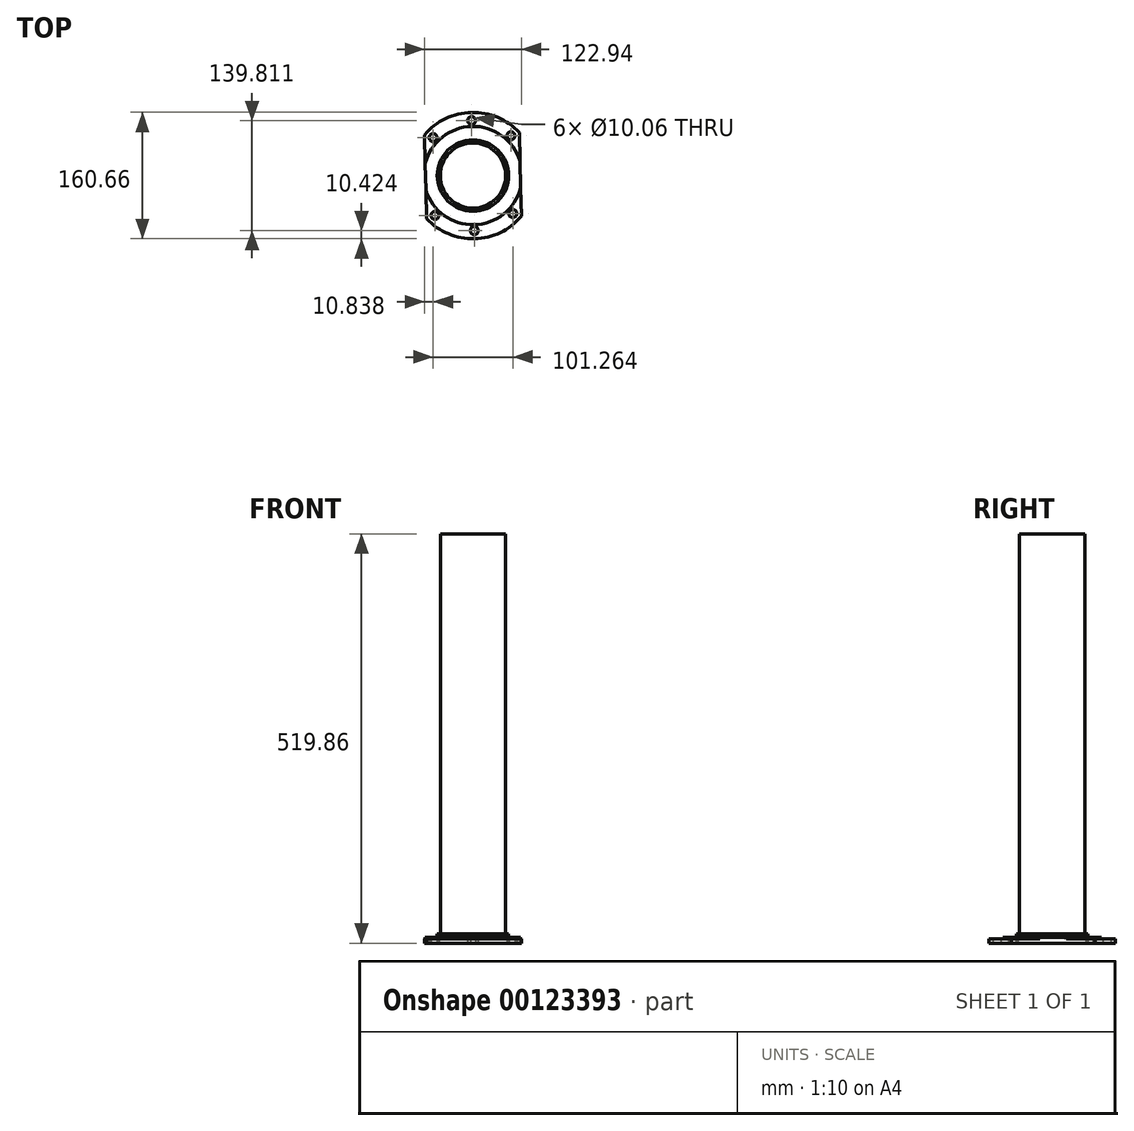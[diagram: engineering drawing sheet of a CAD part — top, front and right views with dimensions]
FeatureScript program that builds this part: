
annotation { "Feature Type Name" : "Feature", "Feature Type Description" : "" }
export const myFeature = defineFeature(function(context is Context, id is Id, definition is map)
    precondition{}
    {
        {
            var Q0;
            Q0=qCreatedBy(makeId("Top.planeOp"),FACE);
            var sketch = newSketch(context, id + "F0", { "sketchPlane" : qUnion([Q0])});
            skCircle(sketch, "E0", {"center": v(0, 0) * mm, "radius": 45.38 * mm, "construction": true});
            skCircle(sketch, "E1", {"center": v(0, 0) * mm, "radius": 69.93 * mm, "construction": true});
            skLineSegment(sketch, "E2", {"start": v(58.89, 54.63) * mm, "end": v(61.47, -51.7) * mm});
            skLineSegment(sketch, "E3", {"start": v(-61.47, 51.7) * mm, "end": v(-58.89, -54.63) * mm});
            skCircle(sketch, "E4", {"center": v(48.23, 50.63) * mm, "radius": 5.03 * mm});
            skCircle(sketch, "E5", {"center": v(-1.7, 69.9) * mm, "radius": 5.03 * mm});
            skCircle(sketch, "E6", {"center": v(-50.63, 48.23) * mm, "radius": 5.03 * mm});
            skCircle(sketch, "E7", {"center": v(50.63, -48.23) * mm, "radius": 5.03 * mm});
            skCircle(sketch, "E8", {"center": v(1.7, -69.9) * mm, "radius": 5.03 * mm});
            skCircle(sketch, "E9", {"center": v(-48.23, -50.63) * mm, "radius": 5.03 * mm});
            skLineSegment(sketch, "E10", {"start": v(48.23, 50.63) * mm, "end": v(50.63, -48.23) * mm, "construction": true});
            skLineSegment(sketch, "E11", {"start": v(-1.7, 69.9) * mm, "end": v(1.7, -69.9) * mm, "construction": true});
            skLineSegment(sketch, "E12", {"start": v(-50.63, 48.23) * mm, "end": v(-48.23, -50.63) * mm, "construction": true});
            skLineSegment(sketch, "E13", {"start": v(48.23, 50.63) * mm, "end": v(-48.23, -50.63) * mm, "construction": true});
            skLineSegment(sketch, "E14", {"start": v(50.63, -48.23) * mm, "end": v(-50.63, 48.23) * mm, "construction": true});
            skArc(sketch, "E15", {"start": v(58.89, 54.63) * mm, "mid": v(-1.95, 80.3) * mm, "end": v(-61.47, 51.7) * mm});
            skArc(sketch, "E16.trimOffspring", {"start": v(-58.89, -54.63) * mm, "mid": v(1.95, -80.3) * mm, "end": v(61.47, -51.7) * mm});
            skSolve(sketch);
        }
        {
            var Q0;
            Q0 = qSketchRegion(id + "F0", true);
            extrude(context, id + "F1", {"entities" : qUnion([Q0]), "depth" : 5.5 * mm});
        }
        {
            var Q0;
            Q0=makeQuery(id+"F1.opExtrude","CAP_FACE",FACE,{"disambiguationData":[OSD([sQuery(id+"F0.wireOp",EDGE,"E2"),sQuery(id+"F0.wireOp",EDGE,"E3"),sQuery(id+"F0.wireOp",EDGE,"E4"),sQuery(id+"F0.wireOp",EDGE,"E5"),sQuery(id+"F0.wireOp",EDGE,"E6"),sQuery(id+"F0.wireOp",EDGE,"E7"),sQuery(id+"F0.wireOp",EDGE,"E8"),sQuery(id+"F0.wireOp",EDGE,"E9"),sQuery(id+"F0.wireOp",EDGE,"E15"),sQuery(id+"F0.wireOp",EDGE,"E16.trimOffspring")])],"isStart":false});
            var sketch = newSketch(context, id + "F2", { "sketchPlane" : qUnion([Q0])});
            skCircle(sketch, "E17", {"center": v(0, 0) * mm, "radius": 45.38 * mm});
            skSolve(sketch);
        }
        {
            var Q0;
            Q0 = qSketchRegion(id + "F2", true);
            extrude(context, id + "F3", {"entities" : qUnion([Q0]), "operationType" : NewBodyOperationType.ADD, "depth" : 6.35 * mm});
        }
        {
            var Q0;
            Q0=makeQuery(id+"F1.opExtrude","CAP_FACE",FACE,{"disambiguationData":[OSD([sQuery(id+"F0.wireOp",EDGE,"E2"),sQuery(id+"F0.wireOp",EDGE,"E3"),sQuery(id+"F0.wireOp",EDGE,"E4"),sQuery(id+"F0.wireOp",EDGE,"E5"),sQuery(id+"F0.wireOp",EDGE,"E6"),sQuery(id+"F0.wireOp",EDGE,"E7"),sQuery(id+"F0.wireOp",EDGE,"E8"),sQuery(id+"F0.wireOp",EDGE,"E9"),sQuery(id+"F0.wireOp",EDGE,"E15"),sQuery(id+"F0.wireOp",EDGE,"E16.trimOffspring")])],"isStart":false});
            var sketch = newSketch(context, id + "F4", { "sketchPlane" : qUnion([Q0])});
            skArc(sketch, "E18", {"start": v(-59.77, -18.44) * mm, "mid": v(1.52, -62.53) * mm, "end": v(60.6, -15.51) * mm});
            skLineSegment(sketch, "E19.0", {"start": v(-60.6, 15.51) * mm, "end": v(-59.77, -18.44) * mm});
            skLineSegment(sketch, "E20.0", {"start": v(59.77, 18.44) * mm, "end": v(60.6, -15.51) * mm});
            skPoint(sketch, "E21.orphan", {"position": v(-61.47, 51.7) * mm});
            skPoint(sketch, "E22.orphan", {"position": v(-58.89, -54.63) * mm});
            skArc(sketch, "E23.trimOffspring", {"start": v(59.77, 18.44) * mm, "mid": v(-1.52, 62.53) * mm, "end": v(-60.6, 15.51) * mm});
            skPoint(sketch, "E24.orphan", {"position": v(58.89, 54.63) * mm});
            skPoint(sketch, "E25.orphan", {"position": v(61.47, -51.7) * mm});
            skSolve(sketch);
        }
        {
            var Q0;
            Q0 = qSketchRegion(id + "F4", true);
            extrude(context, id + "F5", {"entities" : qUnion([Q0]), "operationType" : NewBodyOperationType.ADD, "depth" : 1.78 * mm});
        }
        {
            var Q0;
            Q0=makeQuery(id+"F3.opExtrude","CAP_FACE",FACE,{"disambiguationData":[OSD([sQuery(id+"F2.wireOp",EDGE,"E17")])],"isStart":false});
            var sketch = newSketch(context, id + "F6", { "sketchPlane" : qUnion([Q0])});
            skCircle(sketch, "E26", {"center": v(0, 0) * mm, "radius": 41.5 * mm});
            skSolve(sketch);
        }
        {
            var Q0;
            Q0 = qSketchRegion(id + "F6", true);
            extrude(context, id + "F7", {"entities" : qUnion([Q0]), "operationType" : NewBodyOperationType.ADD, "depth" : 508 * mm});
        }
    });
